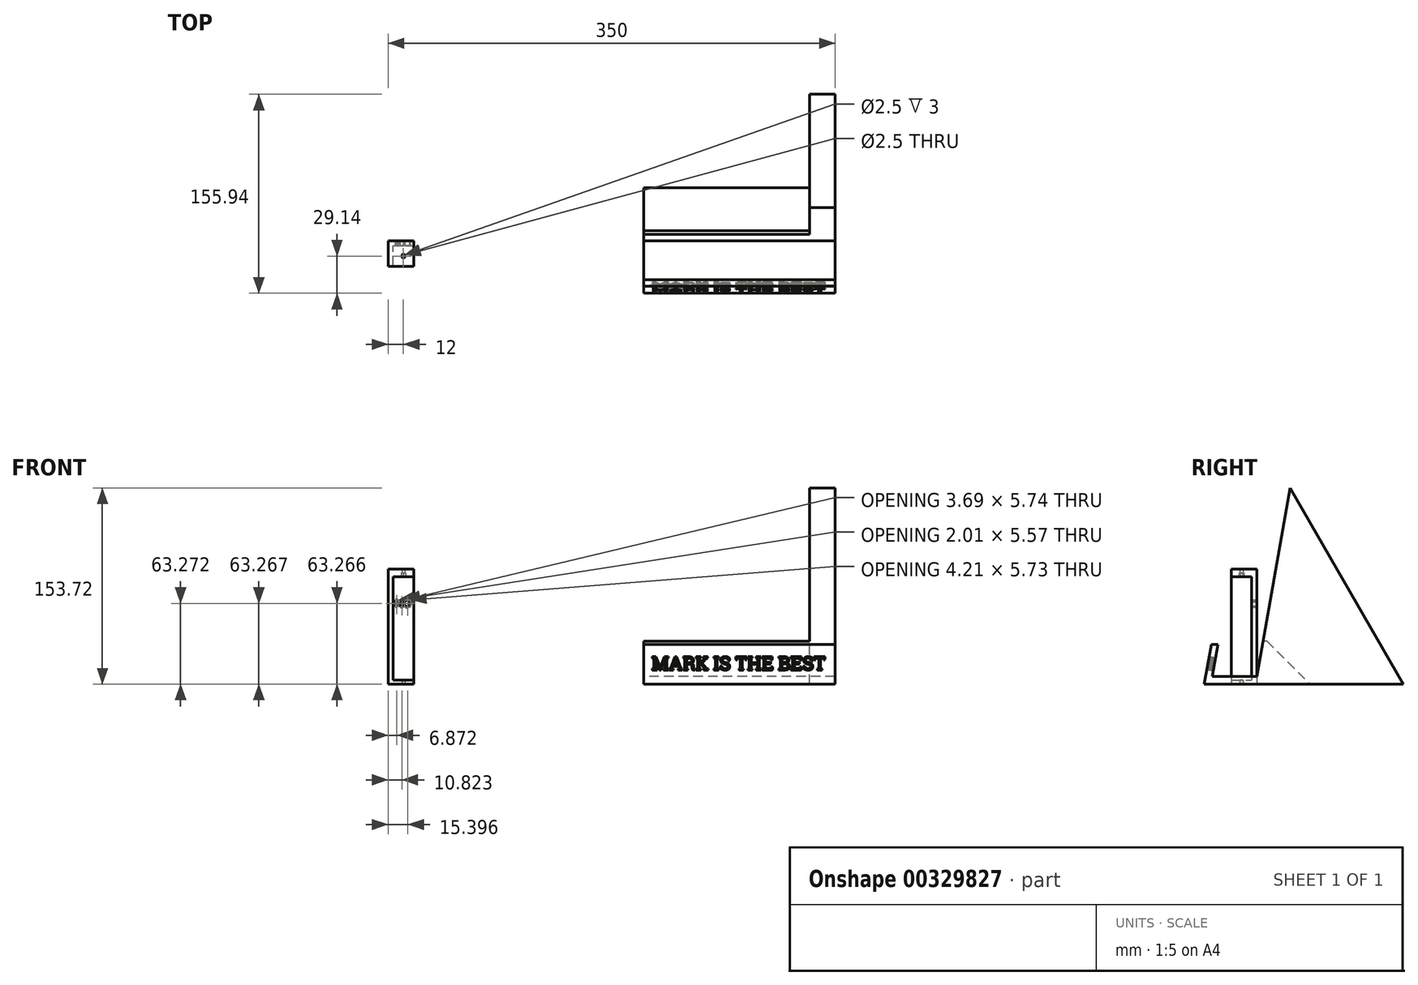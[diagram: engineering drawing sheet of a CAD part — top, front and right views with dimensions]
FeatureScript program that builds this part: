
annotation { "Feature Type Name" : "Feature", "Feature Type Description" : "" }
export const myFeature = defineFeature(function(context is Context, id is Id, definition is map)
    precondition{}
    {
        {
            assignVariable(context, id + "F0", {"name" : "Height", "anyValue" : 90});
        }
        {
            var Q0;
            Q0=qCreatedBy(makeId("Top.planeOp"),FACE);
            var sketch = newSketch(context, id + "F1", { "sketchPlane" : qUnion([Q0])});
            skLineSegment(sketch, "E0", {"start": v(0, 0) * mm, "end": v(20, 0) * mm});
            skLineSegment(sketch, "E1", {"start": v(20, 0) * mm, "end": v(20, -4) * mm});
            skLineSegment(sketch, "E2", {"start": v(20, -4) * mm, "end": v(4, -4) * mm});
            skLineSegment(sketch, "E3", {"start": v(4, -4) * mm, "end": v(4, -20) * mm});
            skLineSegment(sketch, "E4", {"start": v(4, -20) * mm, "end": v(0, -20) * mm});
            skLineSegment(sketch, "E5", {"start": v(0, -20) * mm, "end": v(0, 0) * mm});
            skSolve(sketch);
        }
        {
            var Q0;
            Q0 = qSketchRegion(id + "F1", true);
            var Q1;
            Q1 = qConstructionFilter(qBodyType(qCreatedBy(id + "F1" ,EDGE), BodyType.WIRE), ConstructionObject.NO);
            extrude(context, id + "F2", {"entities" : qUnion([Q0]), "surfaceEntities" : qUnion([Q1]), "depth" : (getVariable(context, 'Height')) * mm});
        }
        {
            var Q0;
            Q0=qCreatedBy(makeId("Top.planeOp"),FACE);
            var sketch = newSketch(context, id + "F3", { "sketchPlane" : qUnion([Q0])});
            skLineSegment(sketch, "E6.bottom", {"start": v(4, -4) * mm, "end": v(20, -4) * mm});
            skLineSegment(sketch, "E6.top", {"start": v(4, -20) * mm, "end": v(20, -20) * mm});
            skLineSegment(sketch, "E6.left", {"start": v(4, -20) * mm, "end": v(4, -4) * mm});
            skLineSegment(sketch, "E6.right", {"start": v(20, -20) * mm, "end": v(20, -4) * mm});
            skCircle(sketch, "E7", {"center": v(12, -12) * mm, "radius": 1.25 * mm});
            skLineSegment(sketch, "E8", {"start": v(12, -12) * mm, "end": v(12, -20) * mm, "construction": true});
            skLineSegment(sketch, "E9", {"start": v(12, -12) * mm, "end": v(20, -12) * mm, "construction": true});
            skSolve(sketch);
        }
        {
            var Q0;
            Q0 = qSketchRegion(id + "F3", true);
            extrude(context, id + "F4", {"entities" : qUnion([Q0]), "operationType" : NewBodyOperationType.ADD, "depth" : 3 * mm});
        }
        {
            var Q0;
            Q0 = qSketchRegion(id + "F3", true);
            extrude(context, id + "F5", {"entities" : qUnion([Q0]), "operationType" : NewBodyOperationType.ADD, "depth" : (getVariable(context, 'Height')) * mm, "hasSecondDirection" : true, "secondDirectionOppositeDirection" : false, "secondDirectionDepth" : (getVariable(context, 'Height') - 6) * mm});
        }
        {
            var Q0;
            Q0=makeQuery(id+"F5.opExtrude","CAP_FACE",FACE,{"disambiguationData":[OSD([sQuery(id+"F3.wireOp",EDGE,"E6.bottom"),sQuery(id+"F3.wireOp",EDGE,"E6.top"),sQuery(id+"F3.wireOp",EDGE,"E6.left"),sQuery(id+"F3.wireOp",EDGE,"E6.right"),sQuery(id+"F3.wireOp",EDGE,"E7")])],"isStart":true});
            var sketch = newSketch(context, id + "F6", { "sketchPlane" : qUnion([Q0])});
            skCircle(sketch, "E10.cCircle", {"center": v(12, 12) * mm, "radius": 1.75 * mm, "construction": true});
            skLineSegment(sketch, "E10.0", {"start": v(10.25, 10.99) * mm, "end": v(10.25, 13.01) * mm});
            skLineSegment(sketch, "E10.1", {"start": v(10.25, 13.01) * mm, "end": v(12, 14.02) * mm});
            skLineSegment(sketch, "E10.2", {"start": v(12, 14.02) * mm, "end": v(13.75, 13.01) * mm});
            skLineSegment(sketch, "E10.3", {"start": v(13.75, 13.01) * mm, "end": v(13.75, 10.99) * mm});
            skLineSegment(sketch, "E10.4", {"start": v(13.75, 10.99) * mm, "end": v(12, 9.98) * mm});
            skLineSegment(sketch, "E10.5", {"start": v(12, 9.98) * mm, "end": v(10.25, 10.99) * mm});
            skPoint(sketch, "E10.0.midPoint", {"position": v(10.25, 12) * mm});
            skSolve(sketch);
        }
        {
            var Q0;
            Q0 = qSketchRegion(id + "F6", true);
            extrude(context, id + "F7", {"entities" : qUnion([Q0]), "operationType" : NewBodyOperationType.REMOVE, "oppositeDirection" : true, "depth" : 3 * mm});
        }
        {
            var Q0;
            Q0=makeQuery(id+"F2.opExtrude","SWEPT_FACE",FACE,{"disambiguationData":[OSD([sQuery(id+"F1.wireOp",EDGE,"E0")])]});
            var sketch = newSketch(context, id + "F8", { "sketchPlane" : qUnion([Q0])});
            skText(sketch, "E11", { "text": "C01", "fontName": "OpenSans-Regular.ttf"});
            const initialGuessF8  = {"E11": [-0.01798, 0.06048, 1, 0, 0.00562]};
            skSetInitialGuess(sketch, initialGuessF8);
            skSolve(sketch);
        }
        {
            var Q0;
            Q0 = qSketchRegion(id + "F8", true);
            extrude(context, id + "F9", {"entities" : qUnion([Q0]), "operationType" : NewBodyOperationType.REMOVE, "endBound" : BoundingType.UP_TO_NEXT, "oppositeDirection" : true, "depth" : 25 * mm});
        }
        {
            var Q0;
            Q0=qCreatedBy(makeId("Right.planeOp"),FACE);
            cPlane(context, id + "F10", {"entities" : qUnion([Q0]), "cplaneType" : CPlaneType.OFFSET, "offset" : 200 * mm, "width" : 150 * mm, "height" : 150 * mm});
        }
        {
            var Q0;
            Q0=qCreatedBy(id+"F10.planeOp",FACE);
            var sketch = newSketch(context, id + "F11", { "sketchPlane" : qUnion([Q0])});
            skLineSegment(sketch, "E12", {"start": v(0, 0) * mm, "end": v(-41.14, 0) * mm});
            skLineSegment(sketch, "E13", {"start": v(-41.14, 0) * mm, "end": v(-35.67, 31) * mm});
            skLineSegment(sketch, "E14", {"start": v(-35.67, 31) * mm, "end": v(-30.6, 31) * mm});
            skLineSegment(sketch, "E15", {"start": v(-30.6, 31) * mm, "end": v(-35, 6) * mm});
            skLineSegment(sketch, "E16", {"start": v(-35, 6) * mm, "end": v(0, 6) * mm});
            skLineSegment(sketch, "E17", {"start": v(0, 6) * mm, "end": v(26.05, 153.72) * mm});
            skLineSegment(sketch, "E18", {"start": v(26.05, 153.72) * mm, "end": v(114.8, 0) * mm});
            skLineSegment(sketch, "E19", {"start": v(114.8, 0) * mm, "end": v(0, 0) * mm});
            skSolve(sketch);
        }
        {
            var Q0;
            Q0 = qSketchRegion(id + "F11", true);
            extrude(context, id + "F12", {"entities" : qUnion([Q0]), "depth" : 150 * mm});
        }
        {
            var Q0;
            Q0=makeQuery(id+"F12.opExtrude","SWEPT_EDGE",EDGE,{"disambiguationData":[OSD([sQuery(id+"F11.wireOp",EDGE,"E17"),sQuery(id+"F11.wireOp",EDGE,"E18")])]});
            cPlane(context, id + "F13", {"entities" : qUnion([Q0]), "cplaneType" : CPlaneType.LINE_ANGLE, "offset" : 25 * mm, "angle" : 90 * degree, "width" : 150 * mm, "height" : 150 * mm});
        }
        {
            var Q0;
            Q0=qCreatedBy(id+"F13.planeOp",FACE);
            var sketch = newSketch(context, id + "F14", { "sketchPlane" : qUnion([Q0])});
            skLineSegment(sketch, "E20.bottom", {"start": v(200, 114.8) * mm, "end": v(330, 114.8) * mm});
            skLineSegment(sketch, "E20.top", {"start": v(200, 0) * mm, "end": v(330, 0) * mm});
            skLineSegment(sketch, "E20.left", {"start": v(200, 114.8) * mm, "end": v(200, 0) * mm});
            skLineSegment(sketch, "E20.right", {"start": v(330, 114.8) * mm, "end": v(330, 0) * mm});
            skSolve(sketch);
        }
        {
            var Q0;
            Q0 = qSketchRegion(id + "F14", true);
            extrude(context, id + "F15", {"entities" : qUnion([Q0]), "operationType" : NewBodyOperationType.REMOVE, "oppositeDirection" : true, "depth" : 120 * mm});
        }
        {
            var Q0;
            Q0=makeQuery(id+"F12.opExtrude","CAP_FACE",FACE,{"disambiguationData":[OSD([sQuery(id+"F11.wireOp",EDGE,"E12"),sQuery(id+"F11.wireOp",EDGE,"E13"),sQuery(id+"F11.wireOp",EDGE,"E14"),sQuery(id+"F11.wireOp",EDGE,"E15"),sQuery(id+"F11.wireOp",EDGE,"E16"),sQuery(id+"F11.wireOp",EDGE,"E17"),sQuery(id+"F11.wireOp",EDGE,"E18"),sQuery(id+"F11.wireOp",EDGE,"E19")])],"isStart":true});
            var sketch = newSketch(context, id + "F16", { "sketchPlane" : qUnion([Q0])});
            skLineSegment(sketch, "E21", {"start": v(-114.8, 0) * mm, "end": v(-95.33, 33.72) * mm});
            skLineSegment(sketch, "E22", {"start": v(-95.33, 33.72) * mm, "end": v(-7.89, 33.72) * mm});
            skLineSegment(sketch, "E23", {"start": v(-7.89, 33.72) * mm, "end": v(-41.6, 0) * mm});
            skLineSegment(sketch, "E24", {"start": v(-41.6, 0) * mm, "end": v(-114.8, 0) * mm});
            skSolve(sketch);
        }
        {
            var Q0;
            Q0 = qSketchRegion(id + "F16", true);
            var Q1;
            Q1=makeQuery(id+"F15.boolean.opBoolean","COPY",FACE,{"derivedFrom":makeQuery(id+"F15.opExtrude","SWEPT_FACE",FACE,{"disambiguationData":[OSD([sQuery(id+"F14.wireOp",EDGE,"E20.right")])]})});
            extrude(context, id + "F17", {"entities" : qUnion([Q0]), "operationType" : NewBodyOperationType.REMOVE, "endBound" : BoundingType.UP_TO_SURFACE, "oppositeDirection" : true, "endBoundEntityFace" : qUnion([Q1]), "depth" : 25 * mm});
        }
        {
            var Q0;
            {var subQ0=sQuery(id+"F14.wireOp",EDGE,"E20.right");Q0=makeQuery(id+"F17.boolean.opBoolean","MERGE",FACE,{"derivedFrom":[makeQuery(id+"F15.boolean.opBoolean","COPY",FACE,{"derivedFrom":makeQuery(id+"F15.opExtrude","SWEPT_FACE",FACE,{"disambiguationData":[OSD([subQ0])]})}),makeQuery(id+"F17.opExtrude","CAP_FACE",FACE,{"disambiguationData":[OSD([subQ0])],"isStart":false})]});}
            var sketch = newSketch(context, id + "F18", { "sketchPlane" : qUnion([Q0])});
            skLineSegment(sketch, "E25.0", {"start": v(-99.2, 9) * mm, "end": v(-30.62, 127.8) * mm});
            skLineSegment(sketch, "E25.1", {"start": v(-45.34, 9) * mm, "end": v(-99.2, 9) * mm});
            skLineSegment(sketch, "E25.2", {"start": v(-45.34, 9) * mm, "end": v(-15.01, 39.32) * mm});
            skLineSegment(sketch, "E25.3", {"start": v(-30.62, 127.8) * mm, "end": v(-15.01, 39.32) * mm});
            skSolve(sketch);
        }
        {
            var Q0;
            Q0=makeQuery(id+"F12.opExtrude","SWEPT_FACE",FACE,{"disambiguationData":[OSD([sQuery(id+"F11.wireOp",EDGE,"E12"),sQuery(id+"F11.wireOp",EDGE,"E19")])]});
            var sketch = newSketch(context, id + "F19", { "sketchPlane" : qUnion([Q0])});
            skLineSegment(sketch, "E26.0", {"start": v(208, 8) * mm, "end": v(208, 27) * mm});
            skLineSegment(sketch, "E26.1", {"start": v(342, 8) * mm, "end": v(208, 8) * mm});
            skLineSegment(sketch, "E26.2", {"start": v(342, 27) * mm, "end": v(342, 8) * mm});
            skLineSegment(sketch, "E26.3", {"start": v(208, 27) * mm, "end": v(342, 27) * mm});
            skLineSegment(sketch, "E27.0", {"start": v(322, -33.6) * mm, "end": v(208, -33.6) * mm});
            skLineSegment(sketch, "E27.1", {"start": v(322, -33.6) * mm, "end": v(322, -12.89) * mm});
            skLineSegment(sketch, "E27.2", {"start": v(322, -12.89) * mm, "end": v(208, -12.89) * mm});
            skLineSegment(sketch, "E27.3", {"start": v(208, -12.89) * mm, "end": v(208, -33.6) * mm});
            skSolve(sketch);
        }
        {
            var Q0;
            Q0=makeQuery(id+"F12.opExtrude","SWEPT_FACE",FACE,{"disambiguationData":[OSD([sQuery(id+"F11.wireOp",EDGE,"E13")])]});
            var sketch = newSketch(context, id + "F20", { "sketchPlane" : qUnion([Q0])});
            skText(sketch, "E28", { "text": "MARK IS THE BEST", "fontName": "RobotoSlab-Regular.ttf"});
            const initialGuessF20  = {"E28": [0.20622, 0.00423, 1, 0, 0.01056]};
            skSetInitialGuess(sketch, initialGuessF20);
            skSolve(sketch);
        }
        {
            var Q0;
            Q0 = qSketchRegion(id + "F20", true);
            extrude(context, id + "F21", {"entities" : qUnion([Q0]), "operationType" : NewBodyOperationType.REMOVE, "oppositeDirection" : true, "depth" : 25 * mm});
        }
    });
